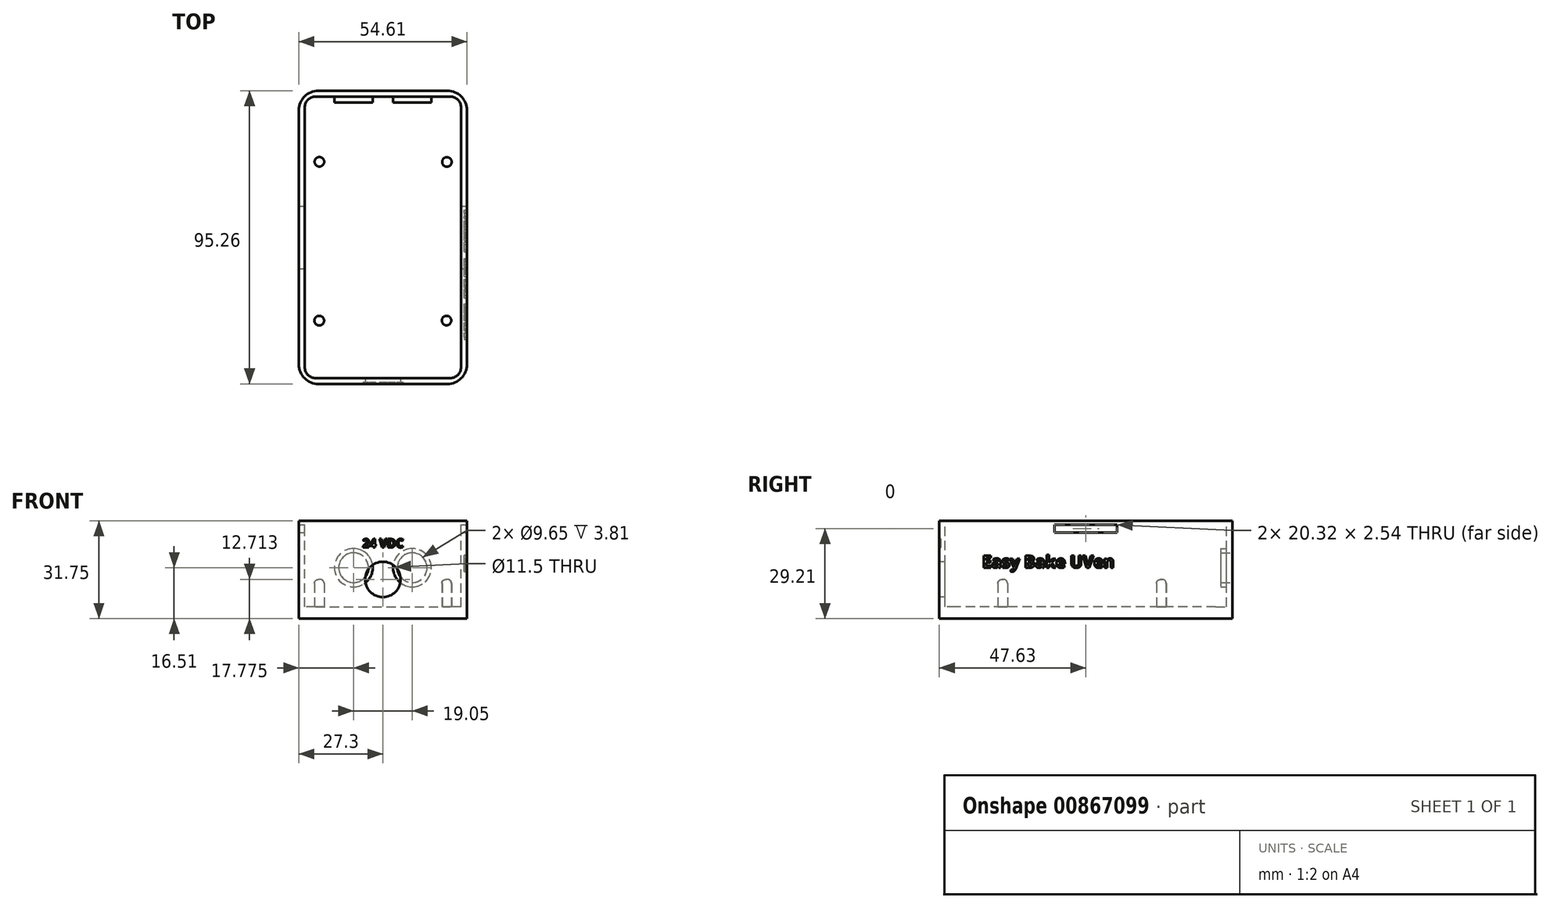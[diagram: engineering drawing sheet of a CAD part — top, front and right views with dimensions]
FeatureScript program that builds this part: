
annotation { "Feature Type Name" : "Feature", "Feature Type Description" : "" }
export const myFeature = defineFeature(function(context is Context, id is Id, definition is map)
    precondition{}
    {
        {
            var Q0;
            Q0=qCreatedBy(makeId("Top.planeOp"),FACE);
            var sketch = newSketch(context, id + "F0", { "sketchPlane" : qUnion([Q0])});
            skLineSegment(sketch, "E0.bottom", {"start": v(20.96, -47.62) * mm, "end": v(-20.95, -47.63) * mm});
            skLineSegment(sketch, "E0.top", {"start": v(20.96, 47.63) * mm, "end": v(-20.95, 47.63) * mm});
            skLineSegment(sketch, "E0.left", {"start": v(27.3, -41.27) * mm, "end": v(27.3, 41.28) * mm});
            skLineSegment(sketch, "E0.right", {"start": v(-27.3, -41.28) * mm, "end": v(-27.3, 41.28) * mm});
            skPoint(sketch, "E0.middle", {"position": v(0, 0) * mm});
            skPoint(sketch, "E1.visualSharp", {"position": v(27.3, -47.62) * mm});
            skArc(sketch, "E1.filletArc", {"start": v(20.96, -47.63) * mm, "mid": v(25.45, -45.77) * mm, "end": v(27.3, -41.27) * mm});
            skPoint(sketch, "E2.visualSharp", {"position": v(27.3, 47.63) * mm});
            skArc(sketch, "E2.filletArc", {"start": v(27.3, 41.28) * mm, "mid": v(25.45, 45.77) * mm, "end": v(20.96, 47.63) * mm});
            skPoint(sketch, "E3.visualSharp", {"position": v(25.53, 38.23) * mm});
            skPoint(sketch, "E4.visualSharp", {"position": v(25.53, -38.23) * mm});
            skPoint(sketch, "E5.visualSharp", {"position": v(-27.3, -47.63) * mm});
            skArc(sketch, "E5.filletArc", {"start": v(-27.3, -41.28) * mm, "mid": v(-25.45, -45.77) * mm, "end": v(-20.95, -47.63) * mm});
            skPoint(sketch, "E6.visualSharp", {"position": v(-27.3, 47.63) * mm});
            skArc(sketch, "E6.filletArc", {"start": v(-20.95, 47.63) * mm, "mid": v(-25.45, 45.77) * mm, "end": v(-27.3, 41.28) * mm});
            skPoint(sketch, "E7.visualSharp", {"position": v(-25.53, 38.23) * mm});
            skPoint(sketch, "E8.visualSharp", {"position": v(-25.53, -38.23) * mm});
            skSolve(sketch);
        }
        {
            var Q0;
            Q0 = qSketchRegion(id + "F0", true);
            extrude(context, id + "F1", {"entities" : qUnion([Q0]), "depth" : 31.75 * mm, "offsetDistance" : 25.4 * mm});
        }
        {
            var Q0;
            Q0=makeQuery(id+"F1.opExtrude","SWEPT_FACE",FACE,{"disambiguationData":[OSD([sQuery(id+"F0.wireOp",EDGE,"E0.bottom")])]});
            var sketch = newSketch(context, id + "F2", { "sketchPlane" : qUnion([Q0])});
            skPoint(sketch, "E9", {"position": v(0, 15.88) * mm});
            skPoint(sketch, "E9.positionSnap0", {"position": v(0, 31.75) * mm});
            skPoint(sketch, "E9.positionSnap1", {"position": v(-20.96, 15.88) * mm});
            skSolve(sketch);
        }
        {
            var Q0;
            Q0=makeQuery(id+"F1.opExtrude","CAP_FACE",FACE,{"disambiguationData":[OSD([sQuery(id+"F0.wireOp",EDGE,"E0.bottom"),sQuery(id+"F0.wireOp",EDGE,"E0.top"),sQuery(id+"F0.wireOp",EDGE,"E0.left"),sQuery(id+"F0.wireOp",EDGE,"E0.right"),sQuery(id+"F0.wireOp",EDGE,"E1.filletArc"),sQuery(id+"F0.wireOp",EDGE,"E2.filletArc"),sQuery(id+"F0.wireOp",EDGE,"E5.filletArc"),sQuery(id+"F0.wireOp",EDGE,"E6.filletArc")])],"isStart":false});
            var sketch = newSketch(context, id + "F3", { "sketchPlane" : qUnion([Q0])});
            skLineSegment(sketch, "E10.bottom", {"start": v(-21.84, 45.72) * mm, "end": v(21.84, 45.72) * mm});
            skLineSegment(sketch, "E10.top", {"start": v(-21.84, -45.72) * mm, "end": v(21.84, -45.72) * mm});
            skLineSegment(sketch, "E10.left", {"start": v(-25.4, 42.16) * mm, "end": v(-25.4, -42.16) * mm});
            skLineSegment(sketch, "E10.right", {"start": v(25.4, 42.16) * mm, "end": v(25.4, -42.16) * mm});
            skPoint(sketch, "E10.middle", {"position": v(0, 0) * mm});
            skPoint(sketch, "E11.visualSharp", {"position": v(-25.4, 45.72) * mm});
            skArc(sketch, "E11.filletArc", {"start": v(-21.84, 45.72) * mm, "mid": v(-24.36, 44.68) * mm, "end": v(-25.4, 42.16) * mm});
            skPoint(sketch, "E12.visualSharp", {"position": v(25.4, 45.72) * mm});
            skArc(sketch, "E12.filletArc", {"start": v(25.4, 42.16) * mm, "mid": v(24.36, 44.68) * mm, "end": v(21.84, 45.72) * mm});
            skPoint(sketch, "E13.visualSharp", {"position": v(25.4, -45.72) * mm});
            skArc(sketch, "E13.filletArc", {"start": v(21.84, -45.72) * mm, "mid": v(24.36, -44.68) * mm, "end": v(25.4, -42.16) * mm});
            skPoint(sketch, "E14.visualSharp", {"position": v(-25.4, -45.72) * mm});
            skArc(sketch, "E14.filletArc", {"start": v(-25.4, -42.16) * mm, "mid": v(-24.36, -44.68) * mm, "end": v(-21.84, -45.72) * mm});
            skSolve(sketch);
        }
        {
            var Q0;
            Q0 = qSketchRegion(id + "F3", true);
            extrude(context, id + "F4", {"entities" : qUnion([Q0]), "operationType" : NewBodyOperationType.REMOVE, "oppositeDirection" : true, "depth" : 27.94 * mm, "offsetDistance" : 25.4 * mm});
        }
        {
            var Q0;
            Q0=makeQuery(id+"F4.boolean.opBoolean","COPY",FACE,{"derivedFrom":makeQuery(id+"F4.opExtrude","CAP_FACE",FACE,{"disambiguationData":[OSD([sQuery(id+"F3.wireOp",EDGE,"E10.bottom"),sQuery(id+"F3.wireOp",EDGE,"E10.top"),sQuery(id+"F3.wireOp",EDGE,"E10.left"),sQuery(id+"F3.wireOp",EDGE,"E10.right"),sQuery(id+"F3.wireOp",EDGE,"E11.filletArc"),sQuery(id+"F3.wireOp",EDGE,"E12.filletArc"),sQuery(id+"F3.wireOp",EDGE,"E13.filletArc"),sQuery(id+"F3.wireOp",EDGE,"E14.filletArc")])],"isStart":false})});
            var sketch = newSketch(context, id + "F5", { "sketchPlane" : qUnion([Q0])});
            skLineSegment(sketch, "E15.bottom", {"start": v(-20.7, 32.13) * mm, "end": v(20.7, 32.13) * mm});
            skLineSegment(sketch, "E15.top", {"start": v(-20.7, -19.43) * mm, "end": v(20.7, -19.43) * mm});
            skLineSegment(sketch, "E15.left", {"start": v(-20.7, 32.13) * mm, "end": v(-20.7, -19.43) * mm});
            skLineSegment(sketch, "E15.right", {"start": v(20.7, 32.13) * mm, "end": v(20.7, -19.43) * mm});
            skPoint(sketch, "E15.middle", {"position": v(0, 0) * mm});
            skPoint(sketch, "E16", {"position": v(20.7, -19.43) * mm});
            skPoint(sketch, "E17", {"position": v(20.7, 32.13) * mm});
            skPoint(sketch, "E18", {"position": v(-20.7, 32.13) * mm});
            skPoint(sketch, "E19", {"position": v(-20.7, -19.43) * mm});
            skSolve(sketch);
        }
        {
            var Q0;
            Q0=makeQuery(id+"F5.imprint","IMPRINT",FACE,{"disambiguationData":[TD([[makeQuery(id+"F5.imprint","IMPRINT",EDGE,{"derivedFrom":sQuery(id+"F5.wireOp",EDGE,"E15.bottom")}),-1.0]])]});
            var sketch = newSketch(context, id + "F6", { "sketchPlane" : qUnion([Q0])});
            skCircle(sketch, "E20", {"center": v(20.8, 21.95) * mm, "radius": 1.55 * mm});
            skCircle(sketch, "E21", {"center": v(20.67, -29.58) * mm, "radius": 1.54 * mm});
            skCircle(sketch, "E22", {"center": v(-20.67, -29.6) * mm, "radius": 1.57 * mm});
            skCircle(sketch, "E23", {"center": v(-20.63, 22) * mm, "radius": 1.56 * mm});
            skSolve(sketch);
        }
        {
            var Q0;
            Q0 = qSketchRegion(id + "F6", true);
            extrude(context, id + "F7", {"entities" : qUnion([Q0]), "depth" : 8.9 * mm, "offsetDistance" : 25.4 * mm});
        }
        {
            var Q0;
            Q0=makeQuery(id+"F7.opExtrude","CAP_FACE",FACE,{"disambiguationData":[OSD([sQuery(id+"F6.wireOp",EDGE,"E20")])],"isStart":false});
            var Q1;
            Q1=makeQuery(id+"F7.opExtrude","CAP_FACE",FACE,{"disambiguationData":[OSD([sQuery(id+"F6.wireOp",EDGE,"E21")])],"isStart":false});
            var Q2;
            Q2=makeQuery(id+"F7.opExtrude","CAP_FACE",FACE,{"disambiguationData":[OSD([sQuery(id+"F6.wireOp",EDGE,"E22")])],"isStart":false});
            var Q3;
            Q3=makeQuery(id+"F7.opExtrude","CAP_FACE",FACE,{"disambiguationData":[OSD([sQuery(id+"F6.wireOp",EDGE,"E23")])],"isStart":false});
            fillet(context, id + "F8", {"entities" : qUnion([Q0, Q1, Q2, Q3]), "radius" : 1.27 * mm, "tangentPropagation" : true, "allowEdgeOverflow" : false});
        }
        {
            var Q0;
            Q0=makeQuery(id+"F1.opExtrude","SWEPT_FACE",FACE,{"disambiguationData":[OSD([sQuery(id+"F0.wireOp",EDGE,"E0.top")])]});
            var sketch = newSketch(context, id + "F9", { "sketchPlane" : qUnion([Q0])});
            skLineSegment(sketch, "E24", {"start": v(0, 15.88) * mm, "end": v(9.53, 15.88) * mm});
            skPoint(sketch, "E24.startSnap0", {"position": v(-20.96, 15.87) * mm});
            skLineSegment(sketch, "E25", {"start": v(0, 15.88) * mm, "end": v(-9.53, 15.88) * mm});
            skPoint(sketch, "E26", {"position": v(-9.53, 16.5) * mm});
            skPoint(sketch, "E27", {"position": v(9.52, 16.5) * mm});
            skCircle(sketch, "E28", {"center": v(-9.53, 16.5) * mm, "radius": 4.83 * mm});
            skCircle(sketch, "E29", {"center": v(9.52, 16.5) * mm, "radius": 4.83 * mm});
            skPoint(sketch, "E30", {"position": v(-9.53, 15.88) * mm});
            skPoint(sketch, "E31", {"position": v(9.53, 15.88) * mm});
            skCircle(sketch, "E32", {"center": v(-9.53, 16.5) * mm, "radius": 6.22 * mm});
            skCircle(sketch, "E33", {"center": v(9.52, 16.5) * mm, "radius": 6.22 * mm});
            skSolve(sketch);
        }
        {
            var Q0;
            Q0=makeQuery(id+"F9.imprint","IMPRINT",FACE,{"disambiguationData":[TD([[makeQuery(id+"F9.imprint","IMPRINT",EDGE,{"derivedFrom":sQuery(id+"F9.wireOp",EDGE,"E28")}),1.0]])]});
            var Q1;
            Q1=makeQuery(id+"F9.imprint","IMPRINT",FACE,{"disambiguationData":[TD([[makeQuery(id+"F9.imprint","IMPRINT",EDGE,{"derivedFrom":sQuery(id+"F9.wireOp",EDGE,"E29")}),1.0]])]});
            extrude(context, id + "F10", {"entities" : qUnion([Q0, Q1]), "operationType" : NewBodyOperationType.REMOVE, "oppositeDirection" : true, "depth" : 11.43 * mm, "offsetDistance" : 25.4 * mm});
        }
        {
            var Q0;
            Q0=makeQuery(id+"F9.imprint","IMPRINT",FACE,{"disambiguationData":[TD([[makeQuery(id+"F9.imprint","IMPRINT",EDGE,{"derivedFrom":sQuery(id+"F9.wireOp",EDGE,"E28")}),-1.0]])]});
            var Q1;
            Q1=makeQuery(id+"F9.imprint","IMPRINT",FACE,{"disambiguationData":[TD([[makeQuery(id+"F9.imprint","IMPRINT",EDGE,{"derivedFrom":sQuery(id+"F9.wireOp",EDGE,"E29")}),-1.0]])]});
            extrude(context, id + "F11", {"entities" : qUnion([Q0, Q1]), "operationType" : NewBodyOperationType.ADD, "oppositeDirection" : true, "depth" : 3.8 * mm, "offsetDistance" : 25.4 * mm});
        }
        {
            var Q0;
            {var subQ0=sQuery(id+"F0.wireOp",EDGE,"E0.bottom");Q0=makeQuery(id+"F2.imprint","IMPRINT",FACE,{"disambiguationData":[TD([[makeQuery(id+"F2.imprint","IMPRINT",EDGE,{"derivedFrom":makeQuery(id+"F1.opExtrude","CAP_EDGE",EDGE,{"disambiguationData":[OSD([subQ0])],"isStart":true})}),-1.0]])]});}
            var sketch = newSketch(context, id + "F12", { "sketchPlane" : qUnion([Q0])});
            skPoint(sketch, "E34", {"position": v(0, 12.71) * mm});
            skCircle(sketch, "E35", {"center": v(0, 12.71) * mm, "radius": 5.75 * mm});
            skSolve(sketch);
        }
        {
            var Q0;
            Q0=makeQuery(id+"F12.imprint","IMPRINT",FACE,{"disambiguationData":[TD([[makeQuery(id+"F12.imprint","IMPRINT",EDGE,{"derivedFrom":sQuery(id+"F12.wireOp",EDGE,"E35")}),1.0]])]});
            var Q1;
            Q1=sQuery(id+"F12.wireOp",EDGE,"E35");
            extrude(context, id + "F13", {"entities" : qUnion([Q0]), "operationType" : NewBodyOperationType.REMOVE, "surfaceEntities" : qUnion([Q1]), "oppositeDirection" : true, "depth" : 3.8 * mm, "offsetDistance" : 25.4 * mm});
        }
        {
            var Q0;
            Q0=makeQuery(id+"F7.opExtrude","SWEPT_BODY",BODY,{"disambiguationData":[OSD([sQuery(id+"F6.wireOp",EDGE,"E22")])]});
            var Q1;
            Q1=makeQuery(id+"F7.opExtrude","SWEPT_BODY",BODY,{"disambiguationData":[OSD([sQuery(id+"F6.wireOp",EDGE,"E21")])]});
            var Q2;
            Q2=makeQuery(id+"F7.opExtrude","SWEPT_BODY",BODY,{"disambiguationData":[OSD([sQuery(id+"F6.wireOp",EDGE,"E20")])]});
            var Q3;
            Q3=makeQuery(id+"F7.opExtrude","SWEPT_BODY",BODY,{"disambiguationData":[OSD([sQuery(id+"F6.wireOp",EDGE,"E23")])]});
            transform(context, id + "F14", {"entities" : qUnion([Q0, Q1, Q2, Q3]), "transformType" : TransformType.TRANSLATION_3D, "dx" : 0 * mm, "dy" : 2.54 * mm, "dz" : 0 * mm, "makeCopy" : false});
        }
        {
            var Q0;
            Q0=makeQuery(id+"F1.opExtrude","SWEPT_FACE",FACE,{"disambiguationData":[OSD([sQuery(id+"F0.wireOp",EDGE,"E0.left")])]});
            var sketch = newSketch(context, id + "F15", { "sketchPlane" : qUnion([Q0])});
            skLineSegment(sketch, "E36.bottom", {"start": v(0, 31.75) * mm, "end": v(-10.16, 31.75) * mm});
            skLineSegment(sketch, "E36.top", {"start": v(0, 30.48) * mm, "end": v(-10.16, 30.48) * mm});
            skLineSegment(sketch, "E36.left", {"start": v(0, 31.75) * mm, "end": v(0, 30.48) * mm});
            skLineSegment(sketch, "E36.right", {"start": v(-10.16, 31.75) * mm, "end": v(-10.16, 30.48) * mm});
            skLineSegment(sketch, "E37.bottom", {"start": v(0, 30.48) * mm, "end": v(10.16, 30.48) * mm});
            skLineSegment(sketch, "E37.top", {"start": v(0, 31.75) * mm, "end": v(10.16, 31.75) * mm});
            skLineSegment(sketch, "E37.left", {"start": v(0, 30.48) * mm, "end": v(0, 31.75) * mm});
            skLineSegment(sketch, "E37.right", {"start": v(10.16, 30.48) * mm, "end": v(10.16, 31.75) * mm});
            skLineSegment(sketch, "E38.bottom", {"start": v(10.16, 30.48) * mm, "end": v(-10.16, 30.48) * mm});
            skLineSegment(sketch, "E38.top", {"start": v(10.16, 27.94) * mm, "end": v(-10.16, 27.94) * mm});
            skLineSegment(sketch, "E38.left", {"start": v(10.16, 30.48) * mm, "end": v(10.16, 27.94) * mm});
            skLineSegment(sketch, "E38.right", {"start": v(-10.16, 30.48) * mm, "end": v(-10.16, 27.94) * mm});
            skSolve(sketch);
        }
        {
            var Q0;
            Q0=makeQuery(id+"F15.imprint","IMPRINT",FACE,{"disambiguationData":[TD([[makeQuery(id+"F15.imprint","IMPRINT",EDGE,{"derivedFrom":sQuery(id+"F15.wireOp",EDGE,"E36.top")}),1.0]])]});
            extrude(context, id + "F16", {"entities" : qUnion([Q0]), "operationType" : NewBodyOperationType.REMOVE, "endBound" : BoundingType.THROUGH_ALL, "oppositeDirection" : true, "depth" : 25.4 * mm, "offsetDistance" : 25.4 * mm});
        }
        {
            var Q0;
            Q0=makeQuery(id+"F1.opExtrude","SWEPT_FACE",FACE,{"disambiguationData":[OSD([sQuery(id+"F0.wireOp",EDGE,"E0.bottom")])]});
            var sketch = newSketch(context, id + "F17", { "sketchPlane" : qUnion([Q0])});
            skText(sketch, "E39", { "text": "24 VDC", "fontName": "OpenSans-Bold.ttf"});
            const initialGuessF17  = {"E39": [-0.00662, 0.02307, 1, 0, 0.0028]};
            skSetInitialGuess(sketch, initialGuessF17);
            skSolve(sketch);
        }
        {
            var Q0;
            Q0 = qSketchRegion(id + "F17", true);
            extrude(context, id + "F18", {"entities" : qUnion([Q0]), "operationType" : NewBodyOperationType.REMOVE, "oppositeDirection" : true, "depth" : .5 * mm, "offsetDistance" : 25.4 * mm});
        }
        {
            var Q0;
            Q0=makeQuery(id+"F1.opExtrude","SWEPT_FACE",FACE,{"disambiguationData":[OSD([sQuery(id+"F0.wireOp",EDGE,"E0.left")])]});
            var sketch = newSketch(context, id + "F19", { "sketchPlane" : qUnion([Q0])});
            skText(sketch, "E40", { "text": "Easy Bake UVen", "fontName": "OpenSans-Bold.ttf"});
            const initialGuessF19  = {"E40": [-0.0337, 0.0165, 1, 0, 0.00392]};
            skSetInitialGuess(sketch, initialGuessF19);
            skSolve(sketch);
        }
        {
            var Q0;
            Q0 = qSketchRegion(id + "F19", true);
            extrude(context, id + "F20", {"entities" : qUnion([Q0]), "operationType" : NewBodyOperationType.REMOVE, "oppositeDirection" : true, "depth" : .85 * mm, "offsetDistance" : 25.4 * mm});
        }
    });
